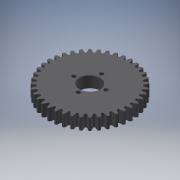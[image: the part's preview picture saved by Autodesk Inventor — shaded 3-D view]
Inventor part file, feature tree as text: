
AUTODESK INVENTOR PART (.ipt)
format: ipt  version: 2016 (Build 200138000, 138)  size: 1,250,816 bytes
history: native  units: mm
features: other x14, sketch x4, revolve x3, extrude x2, hole x1
ambient origin geometry x8: Origin, YZ Plane, XZ Plane, XY Plane, X Axis, Y Axis, Z Axis, Center Point
bodies: Solid1 (feature_tree)
feature tree (24):
  revolve  "Revolution1"  [1 undecoded]
  extrude  "Extrusion1"  TaperAngle=360.0deg  [1 undecoded]
  hole  "Hole1"  [1 undecoded]
  revolve  "Revolution2"  [1 undecoded]
  revolve  "Revolution3"  [1 undecoded]
  other  "b_XY"
  other  "b_YZ"
  other  "b_ZX"
  other  "b_X"
  other  "b_Y"
  other  "b_Z"
  other  "b_Center"
  other  "turn_around_XY"
  other  "turn_around_YZ"
  other  "turn_around_ZX"
  other  "turn_around_X"
  other  "turn_around_Y"
  other  "turn_around_Z"
  other  "turn_around_Center"
  extrude  "押し出し2"  Depth=6.0mm
  sketch  "Sketch_12"  dims[d11=360.0deg d12=0.0mm d13=14.0mm d14=2.0mm d15=2.0mm d16=2.0mm d17=2.0mm d18=6.0mm d19=0.0mm]
  sketch  "Sketch_3"  dims[d0=360.0deg d1=6.0mm d2=0.0mm]
  sketch  "Sketch3"  dims[d3=10.0mm d4=6.0mm d5=4.0mm d6=2.0mm d7=90.0deg d8=6.0mm d9=0.0mm d10=360.0deg]
  sketch  "スケッチ6"
note: 5 required parameter values undecoded (feature->parameter linkage not recoverable at this tier; creation-order binding heuristic only, values carry confidence <= 0.55)